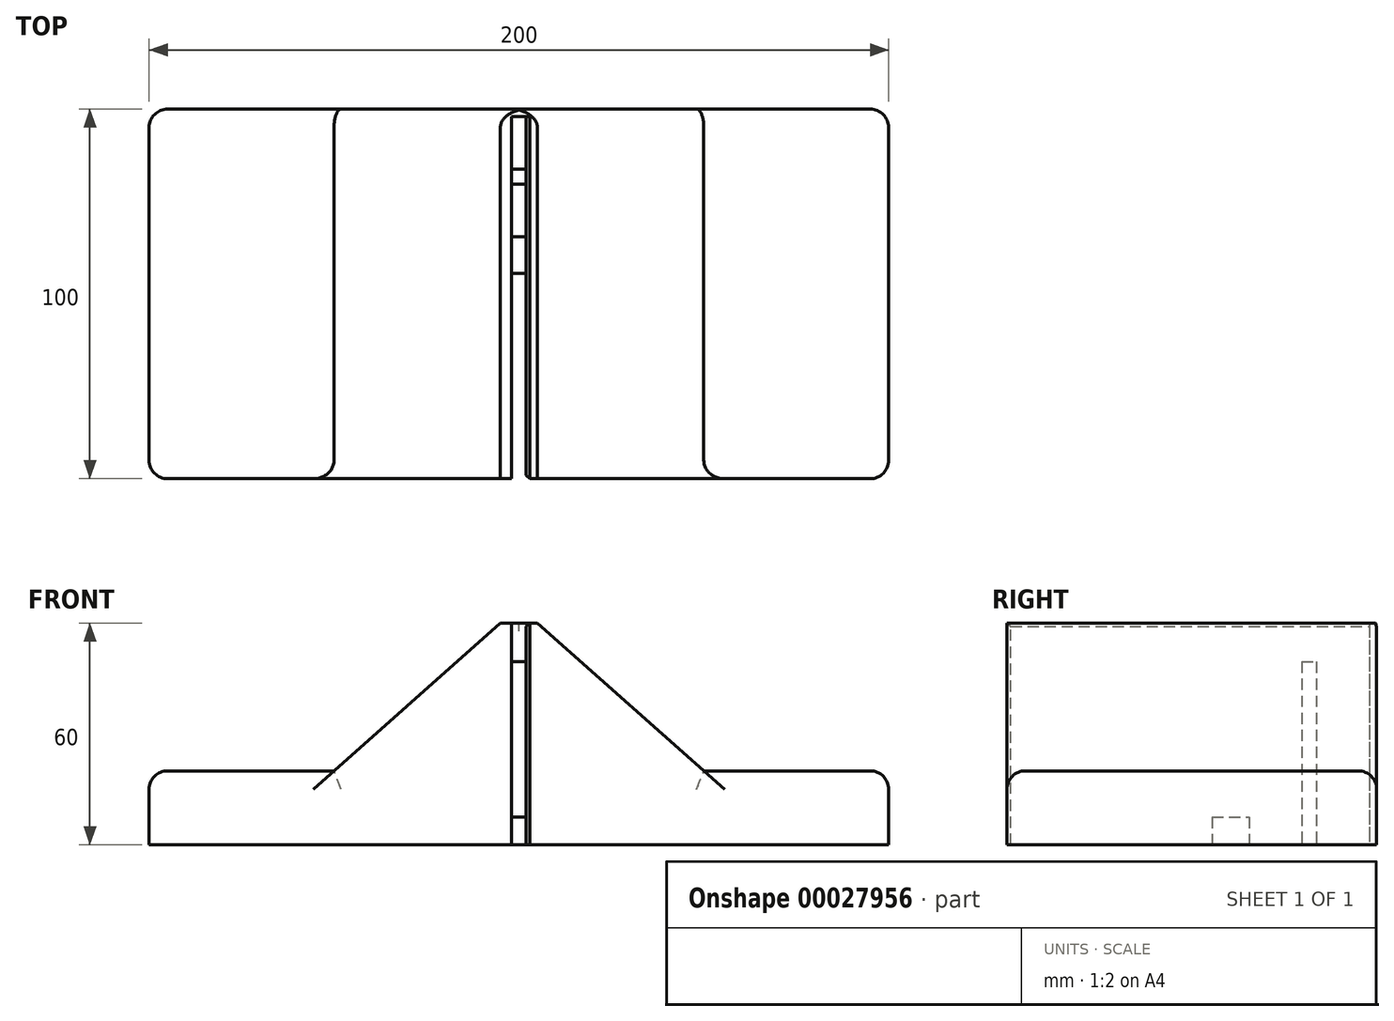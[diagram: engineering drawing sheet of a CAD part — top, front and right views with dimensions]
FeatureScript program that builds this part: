
annotation { "Feature Type Name" : "Feature", "Feature Type Description" : "" }
export const myFeature = defineFeature(function(context is Context, id is Id, definition is map)
    precondition{}
    {
        {
            var Q0;
            Q0=qCreatedBy(makeId("Top.planeOp"),FACE);
            var sketch = newSketch(context, id + "F0", { "sketchPlane" : qUnion([Q0])});
            skLineSegment(sketch, "E0.bottom", {"start": v(-50, 50) * mm, "end": v(50, 50) * mm});
            skLineSegment(sketch, "E0.top", {"start": v(-50, -50) * mm, "end": v(50, -50) * mm});
            skLineSegment(sketch, "E0.left", {"start": v(-50, 50) * mm, "end": v(-50, -50) * mm});
            skLineSegment(sketch, "E0.right", {"start": v(50, 50) * mm, "end": v(50, -50) * mm});
            skLineSegment(sketch, "E1", {"start": v(0, 50) * mm, "end": v(0, -50) * mm, "construction": true});
            skLineSegment(sketch, "E2", {"start": v(50, 0) * mm, "end": v(-50, 0) * mm, "construction": true});
            skSolve(sketch);
        }
        {
            var Q0;
            Q0=makeQuery(id+"F0.imprint","IMPRINT",FACE,{"disambiguationData":[TD([[makeQuery(id+"F0.imprint","IMPRINT",EDGE,{"derivedFrom":sQuery(id+"F0.wireOp",EDGE,"E0.bottom")}),-1.0]])]});
            extrude(context, id + "F1", {"entities" : qUnion([Q0]), "depth" : 60 * mm});
        }
        {
            var Q0;
            Q0=makeQuery(id+"F1.opExtrude","CAP_FACE",FACE,{"disambiguationData":[OSD([sQuery(id+"F0.wireOp",EDGE,"E0.bottom"),sQuery(id+"F0.wireOp",EDGE,"E0.top"),sQuery(id+"F0.wireOp",EDGE,"E0.left"),sQuery(id+"F0.wireOp",EDGE,"E0.right")])],"isStart":false});
            var sketch = newSketch(context, id + "F2", { "sketchPlane" : qUnion([Q0])});
            skLineSegment(sketch, "E3.bottom", {"start": v(-2, 50) * mm, "end": v(2, 50) * mm});
            skLineSegment(sketch, "E3.top", {"start": v(-2, -50) * mm, "end": v(2, -50) * mm});
            skLineSegment(sketch, "E3.left", {"start": v(-2, 50) * mm, "end": v(-2, -50) * mm});
            skLineSegment(sketch, "E3.right", {"start": v(2, 50) * mm, "end": v(2, -50) * mm});
            skLineSegment(sketch, "E4", {"start": v(0, 50) * mm, "end": v(0, -50) * mm, "construction": true});
            skSolve(sketch);
        }
        {
            var Q0;
            Q0=makeQuery(id+"F2.imprint","IMPRINT",FACE,{"disambiguationData":[TD([[makeQuery(id+"F2.imprint","IMPRINT",EDGE,{"derivedFrom":sQuery(id+"F2.wireOp",EDGE,"E3.bottom")}),-1.0]])]});
            extrude(context, id + "F3", {"entities" : qUnion([Q0]), "operationType" : NewBodyOperationType.REMOVE, "endBound" : BoundingType.UP_TO_NEXT, "oppositeDirection" : true, "depth" : 15 * mm});
        }
        {
            var Q0;
            {var subQ0=sQuery(id+"F0.wireOp",EDGE,"E0.bottom");var subQ1=sQuery(id+"F0.wireOp",EDGE,"E0.top");var subQ2=sQuery(id+"F0.wireOp",EDGE,"E0.left");Q0=makeQuery(id+"F3.boolean.opBoolean","SPLIT",FACE,{"disambiguationData":[TD([makeQuery(id+"F1.opExtrude","SWEPT_FACE",FACE,{"disambiguationData":[OSD([subQ2])]})])],"derivedFrom":makeQuery(id+"F1.opExtrude","CAP_FACE",FACE,{"disambiguationData":[OSD([subQ0,subQ1,subQ2,sQuery(id+"F0.wireOp",EDGE,"E0.right")])],"isStart":true})});}
            var sketch = newSketch(context, id + "F4", { "sketchPlane" : qUnion([Q0])});
            skLineSegment(sketch, "E5.bottom", {"start": v(-2, -50) * mm, "end": v(2, -50) * mm});
            skLineSegment(sketch, "E5.top", {"start": v(-2, -48) * mm, "end": v(2, -48) * mm});
            skLineSegment(sketch, "E5.left", {"start": v(-2, -50) * mm, "end": v(-2, -48) * mm});
            skLineSegment(sketch, "E5.right", {"start": v(2, -50) * mm, "end": v(2, -48) * mm});
            skPoint(sketch, "E6.firstSnap0", {"position": v(2, -49) * mm});
            skLineSegment(sketch, "E6.bottom", {"start": v(2, -33.75) * mm, "end": v(-2, -33.75) * mm});
            skLineSegment(sketch, "E6.top", {"start": v(2, -29.75) * mm, "end": v(-2, -29.75) * mm});
            skLineSegment(sketch, "E6.left", {"start": v(2, -33.75) * mm, "end": v(2, -29.75) * mm});
            skLineSegment(sketch, "E6.right", {"start": v(-2, -33.75) * mm, "end": v(-2, -29.75) * mm});
            skLineSegment(sketch, "E7.bottom", {"start": v(2, -15.5) * mm, "end": v(-2, -15.5) * mm});
            skLineSegment(sketch, "E7.top", {"start": v(2, -5.5) * mm, "end": v(-2, -5.5) * mm});
            skLineSegment(sketch, "E7.left", {"start": v(2, -15.5) * mm, "end": v(2, -5.5) * mm});
            skLineSegment(sketch, "E7.right", {"start": v(-2, -15.5) * mm, "end": v(-2, -5.5) * mm});
            skLineSegment(sketch, "E8.0.0", {"start": v(-2, -50) * mm, "end": v(-2, 50) * mm});
            skLineSegment(sketch, "E8.0.1", {"start": v(-2, 50) * mm, "end": v(-50, 50) * mm});
            skLineSegment(sketch, "E8.0.2", {"start": v(-50, 50) * mm, "end": v(-50, -50) * mm});
            skLineSegment(sketch, "E8.0.3", {"start": v(-50, -50) * mm, "end": v(-2, -50) * mm});
            skLineSegment(sketch, "E9.0.0", {"start": v(50, 50) * mm, "end": v(2, 50) * mm});
            skLineSegment(sketch, "E9.0.1", {"start": v(2, 50) * mm, "end": v(2, -50) * mm});
            skLineSegment(sketch, "E9.0.2", {"start": v(2, -50) * mm, "end": v(50, -50) * mm});
            skLineSegment(sketch, "E9.0.3", {"start": v(50, -50) * mm, "end": v(50, 50) * mm});
            skLineSegment(sketch, "E10", {"start": v(-2, -31.75) * mm, "end": v(2, -31.75) * mm, "construction": true});
            skLineSegment(sketch, "E11", {"start": v(-2, -10.5) * mm, "end": v(2, -10.5) * mm, "construction": true});
            skSolve(sketch);
        }
        {
            var Q0;
            {var subQ0=sQuery(id+"F4.wireOp",EDGE,"E7.bottom");Q0=makeQuery(id+"F4.imprint","IMPRINT",FACE,{"disambiguationData":[TD([[makeQuery(id+"F4.imprint","IMPRINT",EDGE,{"derivedFrom":subQ0}),-1.0]])]});}
            var Q1;
            {var subQ0=sQuery(id+"F4.wireOp",EDGE,"E6.bottom");Q1=makeQuery(id+"F4.imprint","IMPRINT",FACE,{"disambiguationData":[TD([[makeQuery(id+"F4.imprint","IMPRINT",EDGE,{"derivedFrom":subQ0}),-1.0]])]});}
            var Q2;
            {var subQ0=sQuery(id+"F4.wireOp",EDGE,"E5.bottom");Q2=makeQuery(id+"F4.imprint","IMPRINT",FACE,{"disambiguationData":[TD([[makeQuery(id+"F4.imprint","IMPRINT",EDGE,{"derivedFrom":subQ0}),1.0]])]});}
            extrude(context, id + "F5", {"entities" : qUnion([Q0, Q1, Q2]), "operationType" : NewBodyOperationType.ADD, "oppositeDirection" : true, "depth" : 7.5 * mm});
        }
        {
            var Q0;
            Q0=makeQuery(id+"F5.opExtrude","CAP_FACE",FACE,{"disambiguationData":[OSD([sQuery(id+"F4.wireOp",EDGE,"E6.bottom"),sQuery(id+"F4.wireOp",EDGE,"E6.top"),sQuery(id+"F4.wireOp",EDGE,"E8.0.0"),sQuery(id+"F4.wireOp",EDGE,"E9.0.1")])],"isStart":false});
            var Q1;
            Q1=makeQuery(id+"F5.opExtrude","CAP_FACE",FACE,{"disambiguationData":[OSD([sQuery(id+"F4.wireOp",EDGE,"E5.bottom"),sQuery(id+"F4.wireOp",EDGE,"E5.top"),sQuery(id+"F4.wireOp",EDGE,"E8.0.0"),sQuery(id+"F4.wireOp",EDGE,"E9.0.1")])],"isStart":false});
            extrude(context, id + "F6", {"entities" : qUnion([Q0, Q1]), "operationType" : NewBodyOperationType.ADD, "depth" : 42 * mm});
        }
        {
            var Q0;
            Q0=makeQuery(id+"F6.opExtrude","CAP_FACE",FACE,{"disambiguationData":[OSD([sQuery(id+"F4.wireOp",EDGE,"E5.bottom"),sQuery(id+"F4.wireOp",EDGE,"E5.top"),sQuery(id+"F4.wireOp",EDGE,"E8.0.0"),sQuery(id+"F4.wireOp",EDGE,"E9.0.1")])],"isStart":false});
            var Q1;
            {var subQ0=sQuery(id+"F0.wireOp",EDGE,"E0.bottom");var subQ1=sQuery(id+"F0.wireOp",EDGE,"E0.top");var subQ2=sQuery(id+"F0.wireOp",EDGE,"E0.left");Q1=makeQuery(id+"F3.boolean.opBoolean","SPLIT",FACE,{"disambiguationData":[TD([makeQuery(id+"F1.opExtrude","SWEPT_FACE",FACE,{"disambiguationData":[OSD([subQ2])]})])],"derivedFrom":makeQuery(id+"F1.opExtrude","CAP_FACE",FACE,{"disambiguationData":[OSD([subQ0,subQ1,subQ2,sQuery(id+"F0.wireOp",EDGE,"E0.right")])],"isStart":false})});}
            extrude(context, id + "F7", {"entities" : qUnion([Q0]), "operationType" : NewBodyOperationType.ADD, "endBound" : BoundingType.UP_TO_SURFACE, "endBoundEntityFace" : qUnion([Q1]), "depth" : 25 * mm});
        }
        {
            var Q0;
            {var subQ1=sQuery(id+"F0.wireOp",EDGE,"E0.left");var subQ2=sQuery(id+"F0.wireOp",EDGE,"E0.top");Q0=makeQuery(id+"F3.boolean.opBoolean","SPLIT",FACE,{"disambiguationData":[TD([makeQuery(id+"F1.opExtrude","SWEPT_FACE",FACE,{"disambiguationData":[OSD([subQ1])]})])],"derivedFrom":makeQuery(id+"F1.opExtrude","SWEPT_FACE",FACE,{"disambiguationData":[OSD([subQ2])]})});}
            var sketch = newSketch(context, id + "F8", { "sketchPlane" : qUnion([Q0])});
            skLineSegment(sketch, "E12", {"start": v(-5, 60) * mm, "end": v(-50, 20) * mm});
            skLineSegment(sketch, "E13", {"start": v(-50, 20) * mm, "end": v(-50, 60) * mm});
            skLineSegment(sketch, "E14", {"start": v(-50, 60) * mm, "end": v(-5, 60) * mm});
            skLineSegment(sketch, "E15.MirrorCS", {"start": v(5, 60) * mm, "end": v(50, 20) * mm});
            skLineSegment(sketch, "E16.MirrorCS", {"start": v(50, 60) * mm, "end": v(5, 60) * mm});
            skLineSegment(sketch, "E17.MirrorCS", {"start": v(50, 20) * mm, "end": v(50, 60) * mm});
            skSolve(sketch);
        }
        {
            var Q0;
            Q0=makeQuery(id+"F8.imprint","IMPRINT",FACE,{"disambiguationData":[TD([[makeQuery(id+"F8.imprint","IMPRINT",EDGE,{"derivedFrom":sQuery(id+"F8.wireOp",EDGE,"E12")}),-1.0]])]});
            var Q1;
            Q1=makeQuery(id+"F8.imprint","IMPRINT",FACE,{"disambiguationData":[TD([[makeQuery(id+"F8.imprint","IMPRINT",EDGE,{"derivedFrom":sQuery(id+"F8.wireOp",EDGE,"E15.MirrorCS")}),1.0]])]});
            extrude(context, id + "F9", {"entities" : qUnion([Q0, Q1]), "operationType" : NewBodyOperationType.REMOVE, "endBound" : BoundingType.THROUGH_ALL, "oppositeDirection" : true, "depth" : 25 * mm});
        }
        {
            var Q0;
            {var subQ0=sQuery(id+"F4.wireOp",EDGE,"E5.bottom");var subQ1=sQuery(id+"F0.wireOp",EDGE,"E0.right");var subQ2=sQuery(id+"F0.wireOp",EDGE,"E0.left");var subQ4=sQuery(id+"F0.wireOp",EDGE,"E0.bottom");var subQ7=makeQuery(id+"F1.opExtrude","SWEPT_FACE",FACE,{"disambiguationData":[OSD([subQ4])]});Q0=makeQuery(id+"F7.boolean.opBoolean","MERGE",FACE,{"derivedFrom":[makeQuery(id+"F6.boolean.opBoolean","MERGE",FACE,{"derivedFrom":[makeQuery(id+"F5.boolean.opBoolean","MERGE",FACE,{"derivedFrom":[makeQuery(id+"F3.boolean.opBoolean","SPLIT",FACE,{"disambiguationData":[TD([makeQuery(id+"F1.opExtrude","SWEPT_FACE",FACE,{"disambiguationData":[OSD([subQ2])]})])],"derivedFrom":subQ7}),makeQuery(id+"F3.boolean.opBoolean","SPLIT",FACE,{"disambiguationData":[TD([makeQuery(id+"F1.opExtrude","SWEPT_FACE",FACE,{"disambiguationData":[OSD([subQ1])]})])],"derivedFrom":subQ7}),makeQuery(id+"F5.opExtrude","SWEPT_FACE",FACE,{"disambiguationData":[OSD([subQ0])]})]}),makeQuery(id+"F6.opExtrude","SWEPT_FACE",FACE,{"disambiguationData":[OSD([subQ0])]})]}),makeQuery(id+"F7.opExtrude","SWEPT_FACE",FACE,{"disambiguationData":[OSD([subQ0])]})]});}
            var sketch = newSketch(context, id + "F10", { "sketchPlane" : qUnion([Q0])});
            skLineSegment(sketch, "E18.bottom", {"start": v(50, 20) * mm, "end": v(100, 20) * mm});
            skLineSegment(sketch, "E18.top", {"start": v(50, 0) * mm, "end": v(100, 0) * mm});
            skLineSegment(sketch, "E18.left", {"start": v(50, 20) * mm, "end": v(50, 0) * mm});
            skLineSegment(sketch, "E18.right", {"start": v(100, 20) * mm, "end": v(100, 0) * mm});
            skLineSegment(sketch, "E19.bottom", {"start": v(-50, 20) * mm, "end": v(-100, 20) * mm});
            skLineSegment(sketch, "E19.top", {"start": v(-50, 0) * mm, "end": v(-100, 0) * mm});
            skLineSegment(sketch, "E19.left", {"start": v(-50, 20) * mm, "end": v(-50, 0) * mm});
            skLineSegment(sketch, "E19.right", {"start": v(-100, 20) * mm, "end": v(-100, 0) * mm});
            skSolve(sketch);
        }
        {
            var Q0;
            Q0=makeQuery(id+"F10.imprint","IMPRINT",FACE,{"disambiguationData":[TD([[makeQuery(id+"F10.imprint","IMPRINT",EDGE,{"derivedFrom":sQuery(id+"F10.wireOp",EDGE,"E18.bottom")}),-1.0]])]});
            var Q1;
            Q1=makeQuery(id+"F10.imprint","IMPRINT",FACE,{"disambiguationData":[TD([[makeQuery(id+"F10.imprint","IMPRINT",EDGE,{"derivedFrom":sQuery(id+"F10.wireOp",EDGE,"E19.bottom")}),1.0]])]});
            var Q2;
            {var subQ0=sQuery(id+"F0.wireOp",EDGE,"E0.right");var subQ2=sQuery(id+"F0.wireOp",EDGE,"E0.top");Q2=makeQuery(id+"F3.boolean.opBoolean","SPLIT",FACE,{"disambiguationData":[TD([makeQuery(id+"F1.opExtrude","SWEPT_FACE",FACE,{"disambiguationData":[OSD([subQ0])]})])],"derivedFrom":makeQuery(id+"F1.opExtrude","SWEPT_FACE",FACE,{"disambiguationData":[OSD([subQ2])]})});}
            extrude(context, id + "F11", {"entities" : qUnion([Q0, Q1]), "operationType" : NewBodyOperationType.ADD, "endBound" : BoundingType.UP_TO_SURFACE, "oppositeDirection" : true, "endBoundEntityFace" : qUnion([Q2]), "depth" : 25 * mm});
        }
        {
            var Q0;
            Q0=makeQuery(id+"F3.boolean.opBoolean","COPY",EDGE,{"derivedFrom":makeQuery(id+"F3.opExtrude","CAP_EDGE",EDGE,{"disambiguationData":[OSD([sQuery(id+"F2.wireOp",EDGE,"E3.left")])],"isStart":true})});
            var Q1;
            Q1=makeQuery(id+"F3.boolean.opBoolean","COPY",EDGE,{"derivedFrom":makeQuery(id+"F3.opExtrude","CAP_EDGE",EDGE,{"disambiguationData":[OSD([sQuery(id+"F2.wireOp",EDGE,"E3.right")])],"isStart":true})});
            var Q2;
            Q2=makeQuery(id+"F3.boolean.opBoolean","COPY",EDGE,{"derivedFrom":makeQuery(id+"F3.opExtrude","SWEPT_EDGE",EDGE,{"disambiguationData":[OSD([sQuery(id+"F0.wireOp",EDGE,"E0.top"),sQuery(id+"F2.wireOp",EDGE,"E3.top"),sQuery(id+"F2.wireOp",EDGE,"E3.left")])]})});
            var Q3;
            Q3=makeQuery(id+"F3.boolean.opBoolean","COPY",EDGE,{"derivedFrom":makeQuery(id+"F3.opExtrude","SWEPT_EDGE",EDGE,{"disambiguationData":[OSD([sQuery(id+"F0.wireOp",EDGE,"E0.top"),sQuery(id+"F2.wireOp",EDGE,"E3.top"),sQuery(id+"F2.wireOp",EDGE,"E3.right")])]})});
            chamfer(context, id + "F12", {"entities" : qUnion([Q0, Q1, Q2, Q3]), "width" : 1 * mm, "tangentPropagation" : true});
        }
        {
            var Q0;
            Q0=makeQuery(id+"F11.opExtrude","SWEPT_EDGE",EDGE,{"disambiguationData":[OSD([sQuery(id+"F10.wireOp",EDGE,"E19.bottom"),sQuery(id+"F10.wireOp",EDGE,"E19.right")])]});
            var Q1;
            Q1=makeQuery(id+"F11.opExtrude","CAP_EDGE",EDGE,{"disambiguationData":[OSD([sQuery(id+"F10.wireOp",EDGE,"E19.right")])],"isStart":true});
            var Q2;
            Q2=makeQuery(id+"F11.opExtrude","CAP_EDGE",EDGE,{"disambiguationData":[OSD([sQuery(id+"F10.wireOp",EDGE,"E19.bottom")])],"isStart":true});
            var Q3;
            {var subQ0=sQuery(id+"F4.wireOp",EDGE,"E5.bottom");var subQ1=sQuery(id+"F0.wireOp",EDGE,"E0.right");var subQ2=sQuery(id+"F0.wireOp",EDGE,"E0.left");var subQ4=sQuery(id+"F0.wireOp",EDGE,"E0.bottom");var subQ7=makeQuery(id+"F1.opExtrude","SWEPT_FACE",FACE,{"disambiguationData":[OSD([subQ4])]});Q3=makeQuery(id+"F9.boolean.opBoolean","INTERSECT",EDGE,{"derivedFrom":[makeQuery(id+"F7.boolean.opBoolean","MERGE",FACE,{"derivedFrom":[makeQuery(id+"F6.boolean.opBoolean","MERGE",FACE,{"derivedFrom":[makeQuery(id+"F5.boolean.opBoolean","MERGE",FACE,{"derivedFrom":[makeQuery(id+"F3.boolean.opBoolean","SPLIT",FACE,{"disambiguationData":[TD([makeQuery(id+"F1.opExtrude","SWEPT_FACE",FACE,{"disambiguationData":[OSD([subQ2])]})])],"derivedFrom":subQ7}),makeQuery(id+"F3.boolean.opBoolean","SPLIT",FACE,{"disambiguationData":[TD([makeQuery(id+"F1.opExtrude","SWEPT_FACE",FACE,{"disambiguationData":[OSD([subQ1])]})])],"derivedFrom":subQ7}),makeQuery(id+"F5.opExtrude","SWEPT_FACE",FACE,{"disambiguationData":[OSD([subQ0])]})]}),makeQuery(id+"F6.opExtrude","SWEPT_FACE",FACE,{"disambiguationData":[OSD([subQ0])]})]}),makeQuery(id+"F7.opExtrude","SWEPT_FACE",FACE,{"disambiguationData":[OSD([subQ0])]})]}),makeQuery(id+"F9.opExtrude","SWEPT_FACE",FACE,{"disambiguationData":[OSD([sQuery(id+"F8.wireOp",EDGE,"E15.MirrorCS")])]})]});}
            var Q4;
            {var subQ0=sQuery(id+"F4.wireOp",EDGE,"E5.bottom");var subQ1=sQuery(id+"F0.wireOp",EDGE,"E0.right");var subQ2=sQuery(id+"F0.wireOp",EDGE,"E0.left");var subQ4=sQuery(id+"F0.wireOp",EDGE,"E0.bottom");var subQ7=makeQuery(id+"F1.opExtrude","SWEPT_FACE",FACE,{"disambiguationData":[OSD([subQ4])]});Q4=makeQuery(id+"F9.boolean.opBoolean","INTERSECT",EDGE,{"derivedFrom":[makeQuery(id+"F7.boolean.opBoolean","MERGE",FACE,{"derivedFrom":[makeQuery(id+"F6.boolean.opBoolean","MERGE",FACE,{"derivedFrom":[makeQuery(id+"F5.boolean.opBoolean","MERGE",FACE,{"derivedFrom":[makeQuery(id+"F3.boolean.opBoolean","SPLIT",FACE,{"disambiguationData":[TD([makeQuery(id+"F1.opExtrude","SWEPT_FACE",FACE,{"disambiguationData":[OSD([subQ2])]})])],"derivedFrom":subQ7}),makeQuery(id+"F3.boolean.opBoolean","SPLIT",FACE,{"disambiguationData":[TD([makeQuery(id+"F1.opExtrude","SWEPT_FACE",FACE,{"disambiguationData":[OSD([subQ1])]})])],"derivedFrom":subQ7}),makeQuery(id+"F5.opExtrude","SWEPT_FACE",FACE,{"disambiguationData":[OSD([subQ0])]})]}),makeQuery(id+"F6.opExtrude","SWEPT_FACE",FACE,{"disambiguationData":[OSD([subQ0])]})]}),makeQuery(id+"F7.opExtrude","SWEPT_FACE",FACE,{"disambiguationData":[OSD([subQ0])]})]}),makeQuery(id+"F9.opExtrude","SWEPT_FACE",FACE,{"disambiguationData":[OSD([sQuery(id+"F8.wireOp",EDGE,"E12")])]})]});}
            var Q5;
            Q5=makeQuery(id+"F11.opExtrude","CAP_EDGE",EDGE,{"disambiguationData":[OSD([sQuery(id+"F10.wireOp",EDGE,"E18.bottom")])],"isStart":true});
            var Q6;
            Q6=makeQuery(id+"F11.opExtrude","CAP_EDGE",EDGE,{"disambiguationData":[OSD([sQuery(id+"F10.wireOp",EDGE,"E18.right")])],"isStart":true});
            var Q7;
            Q7=makeQuery(id+"F11.opExtrude","SWEPT_EDGE",EDGE,{"disambiguationData":[OSD([sQuery(id+"F10.wireOp",EDGE,"E18.bottom"),sQuery(id+"F10.wireOp",EDGE,"E18.right")])]});
            var Q8;
            Q8=makeQuery(id+"F11.opExtrude","CAP_EDGE",EDGE,{"disambiguationData":[OSD([sQuery(id+"F10.wireOp",EDGE,"E18.bottom")])],"isStart":false});
            var Q9;
            Q9=makeQuery(id+"F11.opExtrude","CAP_EDGE",EDGE,{"disambiguationData":[OSD([sQuery(id+"F10.wireOp",EDGE,"E18.right")])],"isStart":false});
            var Q10;
            Q10=makeQuery(id+"F11.opExtrude","CAP_EDGE",EDGE,{"disambiguationData":[OSD([sQuery(id+"F10.wireOp",EDGE,"E19.right")])],"isStart":false});
            var Q11;
            Q11=makeQuery(id+"F11.opExtrude","CAP_EDGE",EDGE,{"disambiguationData":[OSD([sQuery(id+"F10.wireOp",EDGE,"E19.bottom")])],"isStart":false});
            var Q12;
            Q12=makeQuery(id+"F9.boolean.opBoolean","COPY",EDGE,{"derivedFrom":makeQuery(id+"F9.opExtrude","CAP_EDGE",EDGE,{"disambiguationData":[OSD([sQuery(id+"F8.wireOp",EDGE,"E15.MirrorCS")])],"isStart":true})});
            var Q13;
            Q13=makeQuery(id+"F9.boolean.opBoolean","COPY",EDGE,{"derivedFrom":makeQuery(id+"F9.opExtrude","CAP_EDGE",EDGE,{"disambiguationData":[OSD([sQuery(id+"F8.wireOp",EDGE,"E12")])],"isStart":true})});
            fillet(context, id + "F13", {"entities" : qUnion([Q0, Q1, Q2, Q3, Q4, Q5, Q6, Q7, Q8, Q9, Q10, Q11, Q12, Q13]), "radius" : 5 * mm, "tangentPropagation" : true, "allowEdgeOverflow" : false});
        }
    });
